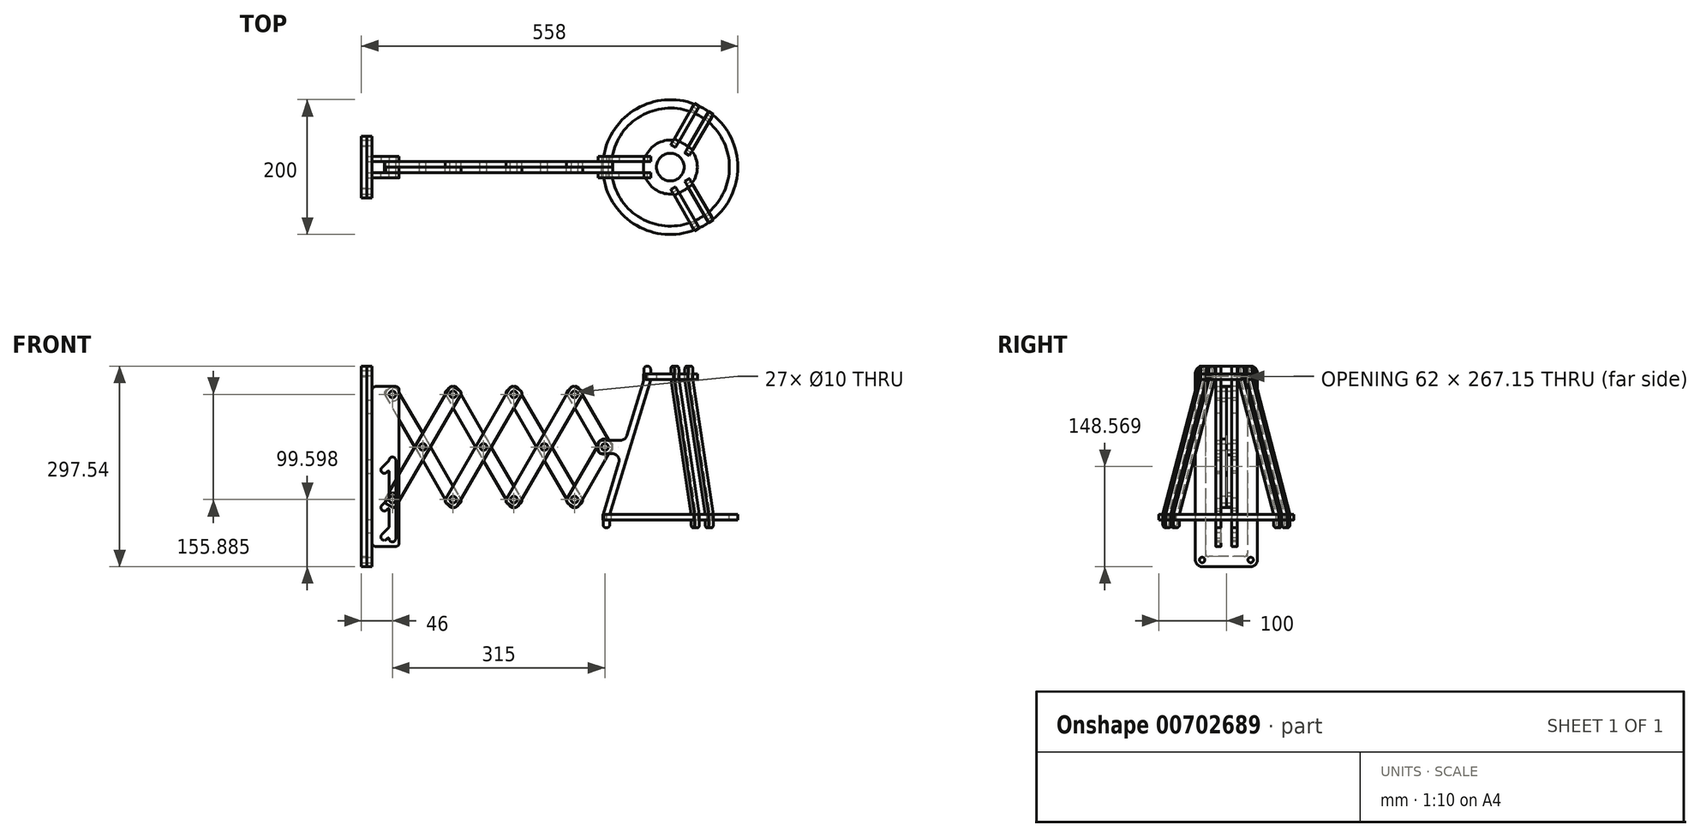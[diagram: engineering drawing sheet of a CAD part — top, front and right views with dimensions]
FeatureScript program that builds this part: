
annotation { "Feature Type Name" : "Feature", "Feature Type Description" : "" }
export const myFeature = defineFeature(function(context is Context, id is Id, definition is map)
    precondition{}
    {
        {
            var Q0;
            Q0=qCreatedBy(makeId("Front.planeOp"),FACE);
            var sketch = newSketch(context, id + "F0", { "sketchPlane" : qUnion([Q0])});
            skLineSegment(sketch, "E0.bottom", {"start": v(54.33, 84.1) * mm, "end": v(45.67, 89.1) * mm});
            skLineSegment(sketch, "E0.top", {"start": v(-45.67, -89.1) * mm, "end": v(-54.33, -84.1) * mm});
            skLineSegment(sketch, "E0.left", {"start": v(56.16, 77.27) * mm, "end": v(-38.84, -87.27) * mm});
            skLineSegment(sketch, "E0.right", {"start": v(38.84, 87.27) * mm, "end": v(-56.16, -77.27) * mm});
            skPoint(sketch, "E0.middle", {"position": v(0, 0) * mm});
            skLineSegment(sketch, "E1", {"start": v(0, 185.82) * mm, "end": v(0, -203.94) * mm, "construction": true});
            skLineSegment(sketch, "E2", {"start": v(-279.88, 0) * mm, "end": v(337.24, 0) * mm, "construction": true});
            skCircle(sketch, "E3", {"center": v(0, 0) * mm, "radius": 5 * mm});
            skCircle(sketch, "E4", {"center": v(45, 77.94) * mm, "radius": 5 * mm});
            skCircle(sketch, "E5.MirrorC", {"center": v(-45, -77.94) * mm, "radius": 5 * mm});
            skPoint(sketch, "E6.visualSharp", {"position": v(41.34, 91.6) * mm});
            skArc(sketch, "E6.filletArc", {"start": v(45.67, 89.1) * mm, "mid": v(41.88, 89.6) * mm, "end": v(38.84, 87.27) * mm});
            skPoint(sketch, "E7.visualSharp", {"position": v(58.66, 81.6) * mm});
            skArc(sketch, "E7.filletArc", {"start": v(56.16, 77.27) * mm, "mid": v(56.66, 81.07) * mm, "end": v(54.33, 84.1) * mm});
            skPoint(sketch, "E8.visualSharp", {"position": v(-41.34, -91.6) * mm});
            skArc(sketch, "E8.filletArc", {"start": v(-45.67, -89.1) * mm, "mid": v(-41.88, -89.6) * mm, "end": v(-38.84, -87.27) * mm});
            skPoint(sketch, "E9.visualSharp", {"position": v(-58.66, -81.6) * mm});
            skArc(sketch, "E9.filletArc", {"start": v(-56.16, -77.27) * mm, "mid": v(-56.66, -81.07) * mm, "end": v(-54.33, -84.1) * mm});
            skSolve(sketch);
        }
        {
            var Q0;
            Q0=makeQuery(id+"F0.imprint","IMPRINT",FACE,{"disambiguationData":[TD([[makeQuery(id+"F0.imprint","IMPRINT",EDGE,{"derivedFrom":sQuery(id+"F0.wireOp",EDGE,"E0.bottom")}),1.0]])]});
            var Q1;
            Q1=makeQuery(id+"F0.imprint","IMPRINT",FACE,{"disambiguationData":[TD([[makeQuery(id+"F0.imprint","IMPRINT",EDGE,{"derivedFrom":sQuery(id+"F0.wireOp",EDGE,"E3")}),-1.0]])]});
            var Q2;
            Q2=makeQuery(id+"F0.imprint","IMPRINT",FACE,{"disambiguationData":[TD([[makeQuery(id+"F0.imprint","IMPRINT",EDGE,{"derivedFrom":sQuery(id+"F0.wireOp",EDGE,"E0.top")}),-1.0]])]});
            var Q3;
            Q3=sQuery(id+"F0.wireOp",EDGE,"E0.right");
            var Q4;
            Q4=sQuery(id+"F0.wireOp",EDGE,"E0.left");
            extrude(context, id + "F1", {"entities" : qUnion([Q0, Q1, Q2]), "surfaceEntities" : qUnion([Q3, Q4]), "depth" : 8 * mm, "offsetDistance" : 25 * mm});
        }
        {
            var Q0;
            Q0=makeQuery(id+"F1.opExtrude","SWEPT_BODY",BODY,{"disambiguationData":[OSD([sQuery(id+"F0.wireOp",EDGE,"E0.bottom"),sQuery(id+"F0.wireOp",EDGE,"E0.top"),sQuery(id+"F0.wireOp",EDGE,"E0.left"),sQuery(id+"F0.wireOp",EDGE,"E0.right"),sQuery(id+"F0.wireOp",EDGE,"E3"),sQuery(id+"F0.wireOp",EDGE,"E4"),sQuery(id+"F0.wireOp",EDGE,"E5.MirrorC"),sQuery(id+"F0.wireOp",EDGE,"E6.filletArc"),sQuery(id+"F0.wireOp",EDGE,"E7.filletArc"),sQuery(id+"F0.wireOp",EDGE,"E8.filletArc"),sQuery(id+"F0.wireOp",EDGE,"E9.filletArc")])]});
            var Q1;
            Q1=qCreatedBy(makeId("Right.planeOp"),FACE);
            mirror(context, id + "F2", {"entities" : qUnion([Q0]), "mirrorPlane" : qUnion([Q1])});
        }
        {
            var Q0;
            Q0=makeQuery(id+"F2.opPattern","COPY",BODY,{"derivedFrom":makeQuery(id+"F1.opExtrude","SWEPT_BODY",BODY,{"disambiguationData":[OSD([sQuery(id+"F0.wireOp",EDGE,"E0.bottom"),sQuery(id+"F0.wireOp",EDGE,"E0.top"),sQuery(id+"F0.wireOp",EDGE,"E0.left"),sQuery(id+"F0.wireOp",EDGE,"E0.right"),sQuery(id+"F0.wireOp",EDGE,"E3"),sQuery(id+"F0.wireOp",EDGE,"E4"),sQuery(id+"F0.wireOp",EDGE,"E5.MirrorC"),sQuery(id+"F0.wireOp",EDGE,"E6.filletArc"),sQuery(id+"F0.wireOp",EDGE,"E7.filletArc"),sQuery(id+"F0.wireOp",EDGE,"E8.filletArc"),sQuery(id+"F0.wireOp",EDGE,"E9.filletArc")])]}),"instanceName":"1"});
            transform(context, id + "F3", {"entities" : qUnion([Q0]), "transformType" : TransformType.TRANSLATION_3D, "dx" : 0 * mm, "dy" : 8 * mm, "dz" : 0 * mm, "makeCopy" : false});
        }
        {
            var Q0;
            Q0=makeQuery(id+"F1.opExtrude","SWEPT_BODY",BODY,{"disambiguationData":[OSD([sQuery(id+"F0.wireOp",EDGE,"E0.bottom"),sQuery(id+"F0.wireOp",EDGE,"E0.top"),sQuery(id+"F0.wireOp",EDGE,"E0.left"),sQuery(id+"F0.wireOp",EDGE,"E0.right"),sQuery(id+"F0.wireOp",EDGE,"E3"),sQuery(id+"F0.wireOp",EDGE,"E4"),sQuery(id+"F0.wireOp",EDGE,"E5.MirrorC"),sQuery(id+"F0.wireOp",EDGE,"E6.filletArc"),sQuery(id+"F0.wireOp",EDGE,"E7.filletArc"),sQuery(id+"F0.wireOp",EDGE,"E8.filletArc"),sQuery(id+"F0.wireOp",EDGE,"E9.filletArc")])]});
            transform(context, id + "F4", {"entities" : qUnion([Q0]), "transformType" : TransformType.TRANSLATION_3D, "dx" : 90 * mm, "dy" : 0 * mm, "dz" : 0 * mm, "makeCopy" : true});
        }
        {
            var Q0;
            Q0=makeQuery(id+"F2.opPattern","COPY",BODY,{"derivedFrom":makeQuery(id+"F1.opExtrude","SWEPT_BODY",BODY,{"disambiguationData":[OSD([sQuery(id+"F0.wireOp",EDGE,"E0.bottom"),sQuery(id+"F0.wireOp",EDGE,"E0.top"),sQuery(id+"F0.wireOp",EDGE,"E0.left"),sQuery(id+"F0.wireOp",EDGE,"E0.right"),sQuery(id+"F0.wireOp",EDGE,"E3"),sQuery(id+"F0.wireOp",EDGE,"E4"),sQuery(id+"F0.wireOp",EDGE,"E5.MirrorC"),sQuery(id+"F0.wireOp",EDGE,"E6.filletArc"),sQuery(id+"F0.wireOp",EDGE,"E7.filletArc"),sQuery(id+"F0.wireOp",EDGE,"E8.filletArc"),sQuery(id+"F0.wireOp",EDGE,"E9.filletArc")])]}),"instanceName":"1"});
            transform(context, id + "F5", {"entities" : qUnion([Q0]), "transformType" : TransformType.TRANSLATION_3D, "dx" : -90 * mm, "dy" : 0 * mm, "dz" : 0 * mm, "makeCopy" : true});
        }
        {
            var Q0;
            Q0=makeQuery(id+"F1.opExtrude","SWEPT_BODY",BODY,{"disambiguationData":[OSD([sQuery(id+"F0.wireOp",EDGE,"E0.bottom"),sQuery(id+"F0.wireOp",EDGE,"E0.top"),sQuery(id+"F0.wireOp",EDGE,"E0.left"),sQuery(id+"F0.wireOp",EDGE,"E0.right"),sQuery(id+"F0.wireOp",EDGE,"E3"),sQuery(id+"F0.wireOp",EDGE,"E4"),sQuery(id+"F0.wireOp",EDGE,"E5.MirrorC"),sQuery(id+"F0.wireOp",EDGE,"E6.filletArc"),sQuery(id+"F0.wireOp",EDGE,"E7.filletArc"),sQuery(id+"F0.wireOp",EDGE,"E8.filletArc"),sQuery(id+"F0.wireOp",EDGE,"E9.filletArc")])]});
            transform(context, id + "F6", {"entities" : qUnion([Q0]), "transformType" : TransformType.TRANSLATION_3D, "dx" : -90 * mm, "dy" : 0 * mm, "dz" : 0 * mm, "makeCopy" : true});
        }
        {
            var Q0;
            Q0=makeQuery(id+"F2.opPattern","COPY",BODY,{"derivedFrom":makeQuery(id+"F1.opExtrude","SWEPT_BODY",BODY,{"disambiguationData":[OSD([sQuery(id+"F0.wireOp",EDGE,"E0.bottom"),sQuery(id+"F0.wireOp",EDGE,"E0.top"),sQuery(id+"F0.wireOp",EDGE,"E0.left"),sQuery(id+"F0.wireOp",EDGE,"E0.right"),sQuery(id+"F0.wireOp",EDGE,"E3"),sQuery(id+"F0.wireOp",EDGE,"E4"),sQuery(id+"F0.wireOp",EDGE,"E5.MirrorC"),sQuery(id+"F0.wireOp",EDGE,"E6.filletArc"),sQuery(id+"F0.wireOp",EDGE,"E7.filletArc"),sQuery(id+"F0.wireOp",EDGE,"E8.filletArc"),sQuery(id+"F0.wireOp",EDGE,"E9.filletArc")])]}),"instanceName":"1"});
            transform(context, id + "F7", {"entities" : qUnion([Q0]), "transformType" : TransformType.TRANSLATION_3D, "dx" : 90 * mm, "dy" : 0 * mm, "dz" : 0 * mm, "makeCopy" : true});
        }
        {
            var Q0;
            Q0=makeQuery(id+"F7.opPattern","COPY",FACE,{"derivedFrom":makeQuery(id+"F2.opPattern","COPY",FACE,{"derivedFrom":makeQuery(id+"F1.opExtrude","CAP_FACE",FACE,{"disambiguationData":[OSD([sQuery(id+"F0.wireOp",EDGE,"E0.bottom"),sQuery(id+"F0.wireOp",EDGE,"E0.top"),sQuery(id+"F0.wireOp",EDGE,"E0.left"),sQuery(id+"F0.wireOp",EDGE,"E0.right"),sQuery(id+"F0.wireOp",EDGE,"E3"),sQuery(id+"F0.wireOp",EDGE,"E4"),sQuery(id+"F0.wireOp",EDGE,"E5.MirrorC"),sQuery(id+"F0.wireOp",EDGE,"E6.filletArc"),sQuery(id+"F0.wireOp",EDGE,"E7.filletArc"),sQuery(id+"F0.wireOp",EDGE,"E8.filletArc"),sQuery(id+"F0.wireOp",EDGE,"E9.filletArc")])],"isStart":true}),"instanceName":"1"}),"instanceName":"1"});
            var sketch = newSketch(context, id + "F8", { "sketchPlane" : qUnion([Q0])});
            skCircle(sketch, "E10.0", {"center": v(135, 77.94) * mm, "radius": 5 * mm});
            skLineSegment(sketch, "E11", {"start": v(130, 89.6) * mm, "end": v(160, 89.6) * mm, "construction": true});
            skPoint(sketch, "E11.startSnap0", {"position": v(41.88, 89.6) * mm});
            skLineSegment(sketch, "E12", {"start": v(22.72, 0) * mm, "end": v(188.2, 0) * mm, "construction": true});
            skLineSegment(sketch, "E13", {"start": v(130, 89.6) * mm, "end": v(160, 89.6) * mm});
            skLineSegment(sketch, "E14", {"start": v(135, 121.8) * mm, "end": v(135, -172.81) * mm, "construction": true});
            skArc(sketch, "E15.0", {"start": v(140, -20) * mm, "mid": v(135, -15) * mm, "end": v(130, -20) * mm});
            skLineSegment(sketch, "E16", {"start": v(95.12, -77.94) * mm, "end": v(188.2, -77.94) * mm, "construction": true});
            skArc(sketch, "E17.MirrorC", {"start": v(140, -135.88) * mm, "mid": v(135, -140.88) * mm, "end": v(130, -135.88) * mm});
            skLineSegment(sketch, "E18", {"start": v(130, -147.54) * mm, "end": v(160, -147.54) * mm});
            skLineSegment(sketch, "E19", {"start": v(125, 84.6) * mm, "end": v(125, -142.54) * mm});
            skLineSegment(sketch, "E20", {"start": v(165, 84.6) * mm, "end": v(165, 69.6) * mm});
            skLineSegment(sketch, "E21", {"start": v(130, -135.88) * mm, "end": v(130, -20) * mm});
            skLineSegment(sketch, "E22.MirrorCS", {"start": v(140, -119.33) * mm, "end": v(140, -92.37) * mm});
            skPoint(sketch, "E23.newPointB", {"position": v(24.22, 89.6) * mm});
            skArc(sketch, "E23.filletArc", {"start": v(130, 89.6) * mm, "mid": v(126.46, 88.14) * mm, "end": v(125, 84.6) * mm});
            skPoint(sketch, "E24.newPointA", {"position": v(188.2, 89.6) * mm});
            skArc(sketch, "E24.filletArc", {"start": v(165, 84.6) * mm, "mid": v(163.54, 88.14) * mm, "end": v(160, 89.6) * mm});
            skPoint(sketch, "E25.visualSharp", {"position": v(125, -147.54) * mm});
            skArc(sketch, "E25.filletArc", {"start": v(125, -142.54) * mm, "mid": v(126.46, -146.08) * mm, "end": v(130, -147.54) * mm});
            skPoint(sketch, "E26.visualSharp", {"position": v(165, -147.54) * mm});
            skArc(sketch, "E26.filletArc", {"start": v(160, -147.54) * mm, "mid": v(163.54, -146.08) * mm, "end": v(165, -142.54) * mm});
            skLineSegment(sketch, "E27", {"start": v(165, 69.6) * mm, "end": v(173, 69.6) * mm});
            skLineSegment(sketch, "E28", {"start": v(173, 69.6) * mm, "end": v(173, 49.6) * mm});
            skLineSegment(sketch, "E29", {"start": v(173, 49.6) * mm, "end": v(165, 49.6) * mm});
            skLineSegment(sketch, "E30", {"start": v(165, -107.54) * mm, "end": v(173, -107.54) * mm});
            skLineSegment(sketch, "E31", {"start": v(173, -107.54) * mm, "end": v(173, -127.54) * mm});
            skLineSegment(sketch, "E32", {"start": v(173, -127.54) * mm, "end": v(165, -127.54) * mm});
            skLineSegment(sketch, "E33.trimOffspring", {"start": v(165, -127.54) * mm, "end": v(165, -142.54) * mm});
            skLineSegment(sketch, "E34.trimOffspring", {"start": v(165, 49.6) * mm, "end": v(165, -18.97) * mm});
            skLineSegment(sketch, "E35", {"start": v(165, -18.97) * mm, "end": v(173, -18.97) * mm});
            skLineSegment(sketch, "E36", {"start": v(173, -18.97) * mm, "end": v(173, -38.97) * mm});
            skLineSegment(sketch, "E37", {"start": v(173, -38.97) * mm, "end": v(165, -38.97) * mm});
            skLineSegment(sketch, "E38.trimOffspring", {"start": v(165, -38.97) * mm, "end": v(165, -107.54) * mm});
            skPoint(sketch, "E39.orphan", {"position": v(165, -28.97) * mm});
            skArc(sketch, "E40", {"start": v(143.5, -93.46) * mm, "mid": v(150.57, -93.46) * mm, "end": v(150.57, -86.4) * mm});
            skLineSegment(sketch, "E41", {"start": v(150.57, -86.4) * mm, "end": v(140, -75.82) * mm});
            skLineSegment(sketch, "E42.MirrorCS", {"start": v(143.5, -93.46) * mm, "end": v(141.7, -91.67) * mm});
            skArc(sketch, "E43.filletArc", {"start": v(141.7, -91.67) * mm, "mid": v(140.62, -91.45) * mm, "end": v(140, -92.37) * mm});
            skArc(sketch, "E44", {"start": v(143.5, -136.97) * mm, "mid": v(150.57, -136.97) * mm, "end": v(150.57, -129.9) * mm});
            skLineSegment(sketch, "E45", {"start": v(150.57, -129.9) * mm, "end": v(140, -119.33) * mm});
            skLineSegment(sketch, "E46.MirrorCS", {"start": v(143.5, -136.97) * mm, "end": v(141.7, -135.18) * mm});
            skArc(sketch, "E47.filletArc", {"start": v(141.7, -135.18) * mm, "mid": v(140.62, -134.96) * mm, "end": v(140, -135.88) * mm});
            skArc(sketch, "E48", {"start": v(143.5, -37.65) * mm, "mid": v(150.57, -37.65) * mm, "end": v(150.57, -30.57) * mm});
            skLineSegment(sketch, "E49", {"start": v(150.57, -30.57) * mm, "end": v(140, -20) * mm});
            skLineSegment(sketch, "E50.MirrorCS", {"start": v(143.5, -37.65) * mm, "end": v(141.7, -35.85) * mm});
            skArc(sketch, "E51.filletArc", {"start": v(141.7, -35.85) * mm, "mid": v(140.62, -35.63) * mm, "end": v(140, -36.56) * mm});
            skLineSegment(sketch, "E52.trimOffspring", {"start": v(140, -75.82) * mm, "end": v(140, -36.56) * mm});
            skSolve(sketch);
        }
        {
            var Q0;
            Q0=qSketchRegion(id+"F8",true);
            extrude(context, id + "F9", {"entities" : qUnion([Q0]), "depth" : 8 * mm, "offsetDistance" : 25 * mm});
        }
        {
            var Q0;
            Q0=makeQuery(id+"F9.opExtrude","SWEPT_BODY",BODY,{"disambiguationData":[OSD([sQuery(id+"F8.wireOp",EDGE,"E10.0"),sQuery(id+"F8.wireOp",EDGE,"E13"),sQuery(id+"F8.wireOp",EDGE,"E15.0"),sQuery(id+"F8.wireOp",EDGE,"E17.MirrorC"),sQuery(id+"F8.wireOp",EDGE,"E18"),sQuery(id+"F8.wireOp",EDGE,"E19"),sQuery(id+"F8.wireOp",EDGE,"E20"),sQuery(id+"F8.wireOp",EDGE,"E21"),sQuery(id+"F8.wireOp",EDGE,"E22.MirrorCS"),sQuery(id+"F8.wireOp",EDGE,"E23.filletArc"),sQuery(id+"F8.wireOp",EDGE,"E24.filletArc"),sQuery(id+"F8.wireOp",EDGE,"E25.filletArc"),sQuery(id+"F8.wireOp",EDGE,"E26.filletArc")])]});
            var Q1;
            Q1=qCreatedBy(makeId("Front.planeOp"),FACE);
            mirror(context, id + "F10", {"entities" : qUnion([Q0]), "mirrorPlane" : qUnion([Q1])});
        }
        {
            var Q0;
            Q0=makeQuery(id+"F9.opExtrude","SWEPT_FACE",FACE,{"disambiguationData":[OSD([sQuery(id+"F8.wireOp",EDGE,"E34.trimOffspring")])]});
            var sketch = newSketch(context, id + "F11", { "sketchPlane" : qUnion([Q0])});
            skPoint(sketch, "E53.middle", {"position": v(0, 0) * mm});
            skLineSegment(sketch, "E54.0.0", {"start": v(-8, 49.6) * mm, "end": v(-8, 69.6) * mm});
            skLineSegment(sketch, "E54.0.1", {"start": v(-8, 69.6) * mm, "end": v(-16, 69.6) * mm});
            skLineSegment(sketch, "E54.0.2", {"start": v(-16, 69.6) * mm, "end": v(-16, 49.6) * mm});
            skLineSegment(sketch, "E54.0.3", {"start": v(-16, 49.6) * mm, "end": v(-8, 49.6) * mm});
            skLineSegment(sketch, "E55.0.0", {"start": v(8, 69.6) * mm, "end": v(8, 49.6) * mm});
            skLineSegment(sketch, "E55.0.1", {"start": v(8, 49.6) * mm, "end": v(16, 49.6) * mm});
            skLineSegment(sketch, "E55.0.2", {"start": v(16, 49.6) * mm, "end": v(16, 69.6) * mm});
            skLineSegment(sketch, "E55.0.3", {"start": v(16, 69.6) * mm, "end": v(8, 69.6) * mm});
            skLineSegment(sketch, "E56.0.0", {"start": v(-8, -38.97) * mm, "end": v(-8, -18.97) * mm});
            skLineSegment(sketch, "E56.0.1", {"start": v(-8, -18.97) * mm, "end": v(-16, -18.97) * mm});
            skLineSegment(sketch, "E56.0.2", {"start": v(-16, -18.97) * mm, "end": v(-16, -38.97) * mm});
            skLineSegment(sketch, "E56.0.3", {"start": v(-16, -38.97) * mm, "end": v(-8, -38.97) * mm});
            skLineSegment(sketch, "E57.0.0", {"start": v(8, -18.97) * mm, "end": v(8, -38.97) * mm});
            skLineSegment(sketch, "E57.0.1", {"start": v(8, -38.97) * mm, "end": v(16, -38.97) * mm});
            skLineSegment(sketch, "E57.0.2", {"start": v(16, -38.97) * mm, "end": v(16, -18.97) * mm});
            skLineSegment(sketch, "E57.0.3", {"start": v(16, -18.97) * mm, "end": v(8, -18.97) * mm});
            skLineSegment(sketch, "E58.0.0", {"start": v(-8, -127.54) * mm, "end": v(-8, -107.54) * mm});
            skLineSegment(sketch, "E58.0.1", {"start": v(-8, -107.54) * mm, "end": v(-16, -107.54) * mm});
            skLineSegment(sketch, "E58.0.2", {"start": v(-16, -107.54) * mm, "end": v(-16, -127.54) * mm});
            skLineSegment(sketch, "E58.0.3", {"start": v(-16, -127.54) * mm, "end": v(-8, -127.54) * mm});
            skLineSegment(sketch, "E59.0.0", {"start": v(8, -107.54) * mm, "end": v(8, -127.54) * mm});
            skLineSegment(sketch, "E59.0.1", {"start": v(8, -127.54) * mm, "end": v(16, -127.54) * mm});
            skLineSegment(sketch, "E59.0.2", {"start": v(16, -127.54) * mm, "end": v(16, -107.54) * mm});
            skLineSegment(sketch, "E59.0.3", {"start": v(16, -107.54) * mm, "end": v(8, -107.54) * mm});
            skLineSegment(sketch, "E60", {"start": v(46, 109.6) * mm, "end": v(46, -167.54) * mm});
            skLineSegment(sketch, "E61", {"start": v(-36, 119.6) * mm, "end": v(36, 119.6) * mm});
            skLineSegment(sketch, "E62", {"start": v(-36, -177.54) * mm, "end": v(36, -177.54) * mm});
            skLineSegment(sketch, "E63.MirrorCS", {"start": v(-46, 109.6) * mm, "end": v(-46, -167.54) * mm});
            skPoint(sketch, "E64.visualSharp", {"position": v(-46, 119.6) * mm});
            skArc(sketch, "E64.filletArc", {"start": v(-36, 119.6) * mm, "mid": v(-43.07, 116.67) * mm, "end": v(-46, 109.6) * mm});
            skPoint(sketch, "E65.visualSharp", {"position": v(46, 119.6) * mm});
            skArc(sketch, "E65.filletArc", {"start": v(46, 109.6) * mm, "mid": v(43.07, 116.67) * mm, "end": v(36, 119.6) * mm});
            skPoint(sketch, "E66.visualSharp", {"position": v(-46, -177.54) * mm});
            skArc(sketch, "E66.filletArc", {"start": v(-46, -167.54) * mm, "mid": v(-43.07, -174.62) * mm, "end": v(-36, -177.54) * mm});
            skPoint(sketch, "E67.visualSharp", {"position": v(46, -177.54) * mm});
            skArc(sketch, "E67.filletArc", {"start": v(36, -177.54) * mm, "mid": v(43.07, -174.62) * mm, "end": v(46, -167.54) * mm});
            skCircle(sketch, "E68", {"center": v(-36, 109.6) * mm, "radius": 4 * mm});
            skCircle(sketch, "E69", {"center": v(36, 109.6) * mm, "radius": 4 * mm});
            skCircle(sketch, "E70", {"center": v(-36, -167.54) * mm, "radius": 4 * mm});
            skCircle(sketch, "E71", {"center": v(36, -167.54) * mm, "radius": 4 * mm});
            skSolve(sketch);
        }
        {
            var Q0;
            Q0=qSketchRegion(id+"F11",true);
            extrude(context, id + "F12", {"entities" : qUnion([Q0]), "depth" : 8 * mm, "offsetDistance" : 25 * mm});
        }
        {
            var Q0;
            Q0=makeQuery(id+"F12.opExtrude","CAP_FACE",FACE,{"disambiguationData":[OSD([sQuery(id+"F11.wireOp",EDGE,"E54.0.0"),sQuery(id+"F11.wireOp",EDGE,"E54.0.1"),sQuery(id+"F11.wireOp",EDGE,"E54.0.2"),sQuery(id+"F11.wireOp",EDGE,"E54.0.3"),sQuery(id+"F11.wireOp",EDGE,"E55.0.0"),sQuery(id+"F11.wireOp",EDGE,"E55.0.1"),sQuery(id+"F11.wireOp",EDGE,"E55.0.2"),sQuery(id+"F11.wireOp",EDGE,"E55.0.3"),sQuery(id+"F11.wireOp",EDGE,"E56.0.0"),sQuery(id+"F11.wireOp",EDGE,"E56.0.1"),sQuery(id+"F11.wireOp",EDGE,"E56.0.2"),sQuery(id+"F11.wireOp",EDGE,"E56.0.3"),sQuery(id+"F11.wireOp",EDGE,"E57.0.0"),sQuery(id+"F11.wireOp",EDGE,"E57.0.1"),sQuery(id+"F11.wireOp",EDGE,"E57.0.2"),sQuery(id+"F11.wireOp",EDGE,"E57.0.3"),sQuery(id+"F11.wireOp",EDGE,"E58.0.0"),sQuery(id+"F11.wireOp",EDGE,"E58.0.1"),sQuery(id+"F11.wireOp",EDGE,"E58.0.2"),sQuery(id+"F11.wireOp",EDGE,"E58.0.3"),sQuery(id+"F11.wireOp",EDGE,"E59.0.0"),sQuery(id+"F11.wireOp",EDGE,"E59.0.1"),sQuery(id+"F11.wireOp",EDGE,"E59.0.2"),sQuery(id+"F11.wireOp",EDGE,"E59.0.3"),sQuery(id+"F11.wireOp",EDGE,"E60"),sQuery(id+"F11.wireOp",EDGE,"E61"),sQuery(id+"F11.wireOp",EDGE,"E62"),sQuery(id+"F11.wireOp",EDGE,"E63.MirrorCS"),sQuery(id+"F11.wireOp",EDGE,"E64.filletArc"),sQuery(id+"F11.wireOp",EDGE,"E65.filletArc"),sQuery(id+"F11.wireOp",EDGE,"E66.filletArc"),sQuery(id+"F11.wireOp",EDGE,"E67.filletArc"),sQuery(id+"F11.wireOp",EDGE,"E68"),sQuery(id+"F11.wireOp",EDGE,"E69"),sQuery(id+"F11.wireOp",EDGE,"E70"),sQuery(id+"F11.wireOp",EDGE,"E71")])],"isStart":false});
            var sketch = newSketch(context, id + "F13", { "sketchPlane" : qUnion([Q0])});
            skArc(sketch, "E72.0.0", {"start": v(-36, 119.6) * mm, "mid": v(-43.07, 116.67) * mm, "end": v(-46, 109.6) * mm});
            skLineSegment(sketch, "E72.0.1", {"start": v(-46, 109.6) * mm, "end": v(-46, -167.54) * mm});
            skArc(sketch, "E72.0.2", {"start": v(-46, -167.54) * mm, "mid": v(-43.07, -174.62) * mm, "end": v(-36, -177.54) * mm});
            skLineSegment(sketch, "E72.0.3", {"start": v(-36, -177.54) * mm, "end": v(36, -177.54) * mm});
            skArc(sketch, "E72.0.4", {"start": v(36, -177.54) * mm, "mid": v(43.07, -174.62) * mm, "end": v(46, -167.54) * mm});
            skLineSegment(sketch, "E72.0.5", {"start": v(46, -167.54) * mm, "end": v(46, 109.6) * mm});
            skArc(sketch, "E72.0.6", {"start": v(46, 109.6) * mm, "mid": v(43.07, 116.67) * mm, "end": v(36, 119.6) * mm});
            skLineSegment(sketch, "E72.0.7", {"start": v(36, 119.6) * mm, "end": v(-36, 119.6) * mm});
            skCircle(sketch, "E73.0", {"center": v(-36, 109.6) * mm, "radius": 4 * mm});
            skCircle(sketch, "E74.0", {"center": v(36, 109.6) * mm, "radius": 4 * mm});
            skCircle(sketch, "E75.0", {"center": v(-36, -167.54) * mm, "radius": 4 * mm});
            skCircle(sketch, "E76.0", {"center": v(36, -167.54) * mm, "radius": 4 * mm});
            skLineSegment(sketch, "E77.bottom", {"start": v(-26, 104.6) * mm, "end": v(26, 104.6) * mm});
            skLineSegment(sketch, "E77.top", {"start": v(-26, -162.54) * mm, "end": v(26, -162.54) * mm});
            skLineSegment(sketch, "E77.left", {"start": v(-31, 99.6) * mm, "end": v(-31, -157.54) * mm});
            skLineSegment(sketch, "E77.right", {"start": v(31, 99.6) * mm, "end": v(31, -157.54) * mm});
            skPoint(sketch, "E78.visualSharp", {"position": v(-31, 104.6) * mm});
            skArc(sketch, "E78.filletArc", {"start": v(-26, 104.6) * mm, "mid": v(-29.54, 103.14) * mm, "end": v(-31, 99.6) * mm});
            skPoint(sketch, "E79.visualSharp", {"position": v(31, 104.6) * mm});
            skArc(sketch, "E79.filletArc", {"start": v(31, 99.6) * mm, "mid": v(29.54, 103.14) * mm, "end": v(26, 104.6) * mm});
            skPoint(sketch, "E80.visualSharp", {"position": v(-31, -162.54) * mm});
            skArc(sketch, "E80.filletArc", {"start": v(-31, -157.54) * mm, "mid": v(-29.54, -161.08) * mm, "end": v(-26, -162.54) * mm});
            skPoint(sketch, "E81.visualSharp", {"position": v(31, -162.54) * mm});
            skArc(sketch, "E81.filletArc", {"start": v(26, -162.54) * mm, "mid": v(29.54, -161.08) * mm, "end": v(31, -157.54) * mm});
            skSolve(sketch);
        }
        {
            var Q0;
            Q0=qSketchRegion(id+"F13",true);
            extrude(context, id + "F14", {"entities" : qUnion([Q0]), "depth" : 8 * mm, "offsetDistance" : 25 * mm});
        }
        {
            var Q0;
            Q0=makeQuery(id+"F6.opPattern","COPY",FACE,{"derivedFrom":makeQuery(id+"F1.opExtrude","CAP_FACE",FACE,{"disambiguationData":[OSD([sQuery(id+"F0.wireOp",EDGE,"E0.bottom"),sQuery(id+"F0.wireOp",EDGE,"E0.top"),sQuery(id+"F0.wireOp",EDGE,"E0.left"),sQuery(id+"F0.wireOp",EDGE,"E0.right"),sQuery(id+"F0.wireOp",EDGE,"E3"),sQuery(id+"F0.wireOp",EDGE,"E4"),sQuery(id+"F0.wireOp",EDGE,"E5.MirrorC"),sQuery(id+"F0.wireOp",EDGE,"E6.filletArc"),sQuery(id+"F0.wireOp",EDGE,"E7.filletArc"),sQuery(id+"F0.wireOp",EDGE,"E8.filletArc"),sQuery(id+"F0.wireOp",EDGE,"E9.filletArc")])],"isStart":true}),"instanceName":"1"});
            var sketch = newSketch(context, id + "F15", { "sketchPlane" : qUnion([Q0])});
            skCircle(sketch, "E82.0", {"center": v(135, -77.94) * mm, "radius": 5 * mm});
            skCircle(sketch, "E83", {"center": v(135, -77.94) * mm, "radius": 10 * mm});
            skSolve(sketch);
        }
        {
            var Q0;
            Q0=qSketchRegion(id+"F15",true);
            extrude(context, id + "F16", {"entities" : qUnion([Q0]), "depth" : 8 * mm, "offsetDistance" : 25 * mm});
        }
        {
            var Q0;
            Q0=makeQuery(id+"F5.opPattern","COPY",FACE,{"derivedFrom":makeQuery(id+"F2.opPattern","COPY",FACE,{"derivedFrom":makeQuery(id+"F1.opExtrude","CAP_FACE",FACE,{"disambiguationData":[OSD([sQuery(id+"F0.wireOp",EDGE,"E0.bottom"),sQuery(id+"F0.wireOp",EDGE,"E0.top"),sQuery(id+"F0.wireOp",EDGE,"E0.left"),sQuery(id+"F0.wireOp",EDGE,"E0.right"),sQuery(id+"F0.wireOp",EDGE,"E3"),sQuery(id+"F0.wireOp",EDGE,"E4"),sQuery(id+"F0.wireOp",EDGE,"E5.MirrorC"),sQuery(id+"F0.wireOp",EDGE,"E6.filletArc"),sQuery(id+"F0.wireOp",EDGE,"E7.filletArc"),sQuery(id+"F0.wireOp",EDGE,"E8.filletArc"),sQuery(id+"F0.wireOp",EDGE,"E9.filletArc")])],"isStart":false}),"instanceName":"1"}),"instanceName":"1"});
            var sketch = newSketch(context, id + "F17", { "sketchPlane" : qUnion([Q0])});
            skCircle(sketch, "E84.0", {"center": v(-135, 77.94) * mm, "radius": 5 * mm});
            skCircle(sketch, "E85", {"center": v(-135, 77.94) * mm, "radius": 10 * mm});
            skSolve(sketch);
        }
        {
            var Q0;
            Q0=qSketchRegion(id+"F17",true);
            extrude(context, id + "F18", {"entities" : qUnion([Q0]), "depth" : 8 * mm, "offsetDistance" : 25 * mm});
        }
        {
            var Q0;
            Q0=makeQuery(id+"F2.opPattern","COPY",FACE,{"derivedFrom":makeQuery(id+"F1.opExtrude","CAP_FACE",FACE,{"disambiguationData":[OSD([sQuery(id+"F0.wireOp",EDGE,"E0.bottom"),sQuery(id+"F0.wireOp",EDGE,"E0.top"),sQuery(id+"F0.wireOp",EDGE,"E0.left"),sQuery(id+"F0.wireOp",EDGE,"E0.right"),sQuery(id+"F0.wireOp",EDGE,"E3"),sQuery(id+"F0.wireOp",EDGE,"E4"),sQuery(id+"F0.wireOp",EDGE,"E5.MirrorC"),sQuery(id+"F0.wireOp",EDGE,"E6.filletArc"),sQuery(id+"F0.wireOp",EDGE,"E7.filletArc"),sQuery(id+"F0.wireOp",EDGE,"E8.filletArc"),sQuery(id+"F0.wireOp",EDGE,"E9.filletArc")])],"isStart":false}),"instanceName":"1"});
            var sketch = newSketch(context, id + "F19", { "sketchPlane" : qUnion([Q0])});
            skLineSegment(sketch, "E86.top", {"start": v(134.33, -89.1) * mm, "end": v(125.67, -84.1) * mm});
            skLineSegment(sketch, "E86.left", {"start": v(191.55, 0) * mm, "end": v(141.16, -87.27) * mm});
            skLineSegment(sketch, "E86.right", {"start": v(173.84, 9.33) * mm, "end": v(123.84, -77.27) * mm});
            skPoint(sketch, "E86.middle", {"position": v(180, 0) * mm});
            skLineSegment(sketch, "E87", {"start": v(180, 185.82) * mm, "end": v(180, -203.94) * mm, "construction": true});
            skLineSegment(sketch, "E88", {"start": v(-99.88, 0) * mm, "end": v(517.24, 0) * mm, "construction": true});
            skCircle(sketch, "E89.MirrorC", {"center": v(135, -77.94) * mm, "radius": 5 * mm});
            skPoint(sketch, "E90.visualSharp", {"position": v(138.66, -91.6) * mm});
            skArc(sketch, "E90.filletArc", {"start": v(134.33, -89.1) * mm, "mid": v(138.12, -89.6) * mm, "end": v(141.16, -87.27) * mm});
            skPoint(sketch, "E91.visualSharp", {"position": v(121.34, -81.6) * mm});
            skArc(sketch, "E91.filletArc", {"start": v(123.84, -77.27) * mm, "mid": v(123.34, -81.07) * mm, "end": v(125.67, -84.1) * mm});
            skLineSegment(sketch, "E92.bottom", {"start": v(189.33, 6.16) * mm, "end": v(180.67, 11.16) * mm});
            skCircle(sketch, "E93", {"center": v(180, 0) * mm, "radius": 5 * mm});
            skArc(sketch, "E94.filletArc", {"start": v(180.67, 11.16) * mm, "mid": v(176.88, 11.66) * mm, "end": v(173.84, 9.33) * mm});
            skArc(sketch, "E95.filletArc", {"start": v(191.16, -0.67) * mm, "mid": v(191.66, 3.12) * mm, "end": v(189.33, 6.16) * mm});
            skSolve(sketch);
        }
        {
            var Q0;
            Q0=qSketchRegion(id+"F19",true);
            extrude(context, id + "F20", {"entities" : qUnion([Q0]), "operationType" : NewBodyOperationType.ADD, "depth" : 8 * mm, "offsetDistance" : 25 * mm});
        }
        {
            var Q0;
            Q0=makeQuery(id+"F4.opPattern","COPY",FACE,{"derivedFrom":makeQuery(id+"F1.opExtrude","CAP_FACE",FACE,{"disambiguationData":[OSD([sQuery(id+"F0.wireOp",EDGE,"E0.bottom"),sQuery(id+"F0.wireOp",EDGE,"E0.top"),sQuery(id+"F0.wireOp",EDGE,"E0.left"),sQuery(id+"F0.wireOp",EDGE,"E0.right"),sQuery(id+"F0.wireOp",EDGE,"E3"),sQuery(id+"F0.wireOp",EDGE,"E4"),sQuery(id+"F0.wireOp",EDGE,"E5.MirrorC"),sQuery(id+"F0.wireOp",EDGE,"E6.filletArc"),sQuery(id+"F0.wireOp",EDGE,"E7.filletArc"),sQuery(id+"F0.wireOp",EDGE,"E8.filletArc"),sQuery(id+"F0.wireOp",EDGE,"E9.filletArc")])],"isStart":true}),"instanceName":"1"});
            var sketch = newSketch(context, id + "F21", { "sketchPlane" : qUnion([Q0])});
            skLineSegment(sketch, "E96.top", {"start": v(-180.67, -11.16) * mm, "end": v(-189.33, -6.16) * mm});
            skLineSegment(sketch, "E96.left", {"start": v(-123.45, 77.94) * mm, "end": v(-173.84, -9.33) * mm});
            skLineSegment(sketch, "E96.right", {"start": v(-141.16, 87.27) * mm, "end": v(-191.16, 0.67) * mm});
            skPoint(sketch, "E96.middle", {"position": v(-135, 77.94) * mm});
            skLineSegment(sketch, "E97", {"start": v(-135, 263.76) * mm, "end": v(-135, -126) * mm, "construction": true});
            skLineSegment(sketch, "E98", {"start": v(-414.88, 77.94) * mm, "end": v(202.24, 77.94) * mm, "construction": true});
            skCircle(sketch, "E99.MirrorC", {"center": v(-180, 0) * mm, "radius": 5 * mm});
            skPoint(sketch, "E100.visualSharp", {"position": v(-176.34, -13.66) * mm});
            skArc(sketch, "E100.filletArc", {"start": v(-180.67, -11.16) * mm, "mid": v(-176.88, -11.66) * mm, "end": v(-173.84, -9.33) * mm});
            skPoint(sketch, "E101.visualSharp", {"position": v(-193.66, -3.66) * mm});
            skArc(sketch, "E101.filletArc", {"start": v(-191.16, 0.67) * mm, "mid": v(-191.66, -3.12) * mm, "end": v(-189.33, -6.16) * mm});
            skLineSegment(sketch, "E102.bottom", {"start": v(-125.67, 84.1) * mm, "end": v(-134.33, 89.1) * mm});
            skCircle(sketch, "E103", {"center": v(-135, 77.94) * mm, "radius": 5 * mm});
            skArc(sketch, "E104.filletArc", {"start": v(-134.33, 89.1) * mm, "mid": v(-138.12, 89.6) * mm, "end": v(-141.16, 87.27) * mm});
            skArc(sketch, "E105.filletArc", {"start": v(-123.84, 77.27) * mm, "mid": v(-123.34, 81.07) * mm, "end": v(-125.67, 84.1) * mm});
            skSolve(sketch);
        }
        {
            var Q0;
            Q0=qSketchRegion(id+"F21",true);
            extrude(context, id + "F22", {"entities" : qUnion([Q0]), "depth" : 8 * mm, "offsetDistance" : 25 * mm});
        }
        {
            var Q0;
            Q0=qCreatedBy(makeId("Top.planeOp"),FACE);
            cPlane(context, id + "F23", {"entities" : qUnion([Q0]), "cplaneType" : CPlaneType.OFFSET, "offset" : 100 * mm, "width" : 150 * mm, "height" : 150 * mm});
        }
        {
            var Q0;
            Q0=qCreatedBy(id+"F23.planeOp",FACE);
            var sketch = newSketch(context, id + "F24", { "sketchPlane" : qUnion([Q0])});
            skLineSegment(sketch, "E106", {"start": v(275, -71.82) * mm, "end": v(275, 43.7) * mm, "construction": true});
            skCircle(sketch, "E107", {"center": v(275, 0) * mm, "radius": 20.5 * mm});
            skLineSegment(sketch, "E108", {"start": v(166.47, 0) * mm, "end": v(330.06, 0) * mm, "construction": true});
            skLineSegment(sketch, "E109", {"start": v(235.8, -8) * mm, "end": v(240.8, -8) * mm});
            skLineSegment(sketch, "E110", {"start": v(240.8, -8) * mm, "end": v(240.8, -16) * mm});
            skLineSegment(sketch, "E111", {"start": v(240.8, -16) * mm, "end": v(238.34, -16) * mm});
            skLineSegment(sketch, "E112.MirrorCS", {"start": v(235.8, 8) * mm, "end": v(240.8, 8) * mm});
            skLineSegment(sketch, "E113.MirrorCS", {"start": v(240.8, 8) * mm, "end": v(240.8, 16) * mm});
            skLineSegment(sketch, "E114.MirrorCS", {"start": v(240.8, 16) * mm, "end": v(238.34, 16) * mm});
            skLineSegment(sketch, "E115.1.1", {"start": v(285.17, -33.61) * mm, "end": v(278.24, -37.61) * mm});
            skLineSegment(sketch, "E115.1.2", {"start": v(287.67, -37.94) * mm, "end": v(285.17, -33.61) * mm});
            skLineSegment(sketch, "E115.1.3", {"start": v(278.24, -37.61) * mm, "end": v(279.47, -39.75) * mm});
            skLineSegment(sketch, "E115.1.4", {"start": v(305.95, -21.61) * mm, "end": v(307.19, -23.75) * mm});
            skLineSegment(sketch, "E115.1.5", {"start": v(299.02, -25.61) * mm, "end": v(305.95, -21.61) * mm});
            skLineSegment(sketch, "E115.1.6", {"start": v(301.52, -29.94) * mm, "end": v(299.02, -25.61) * mm});
            skLineSegment(sketch, "E115.2.1", {"start": v(299.02, 25.61) * mm, "end": v(305.95, 21.61) * mm});
            skLineSegment(sketch, "E115.2.2", {"start": v(301.52, 29.94) * mm, "end": v(299.02, 25.61) * mm});
            skLineSegment(sketch, "E115.2.3", {"start": v(305.95, 21.61) * mm, "end": v(307.19, 23.75) * mm});
            skLineSegment(sketch, "E115.2.4", {"start": v(278.24, 37.61) * mm, "end": v(279.47, 39.75) * mm});
            skLineSegment(sketch, "E115.2.5", {"start": v(285.17, 33.61) * mm, "end": v(278.24, 37.61) * mm});
            skLineSegment(sketch, "E115.2.6", {"start": v(287.67, 37.94) * mm, "end": v(285.17, 33.61) * mm});
            skArc(sketch, "E116", {"start": v(279.47, 39.75) * mm, "mid": v(255, 34.64) * mm, "end": v(238.34, 16) * mm});
            skArc(sketch, "E117.trimOffspring", {"start": v(301.52, 29.94) * mm, "mid": v(295, 34.64) * mm, "end": v(287.67, 37.94) * mm});
            skArc(sketch, "E118.trimOffspring", {"start": v(307.19, -23.75) * mm, "mid": v(315, 0) * mm, "end": v(307.19, 23.75) * mm});
            skArc(sketch, "E119.trimOffspring", {"start": v(287.67, -37.94) * mm, "mid": v(295, -34.64) * mm, "end": v(301.52, -29.94) * mm});
            skArc(sketch, "E120.trimOffspring", {"start": v(238.34, -16) * mm, "mid": v(255, -34.64) * mm, "end": v(279.47, -39.75) * mm});
            skArc(sketch, "E121.trimOffspring", {"start": v(235.8, 8) * mm, "mid": v(235, 0) * mm, "end": v(235.8, -8) * mm});
            skLineSegment(sketch, "E122.0", {"start": v(185, 8) * mm, "end": v(175, 8) * mm, "construction": true});
            skLineSegment(sketch, "E123", {"start": v(185, 8) * mm, "end": v(185, -8) * mm, "construction": true});
            skLineSegment(sketch, "E124", {"start": v(185, -8) * mm, "end": v(175, -8) * mm, "construction": true});
            skLineSegment(sketch, "E125", {"start": v(175, -8) * mm, "end": v(175, 8) * mm, "construction": true});
            skSolve(sketch);
        }
        {
            var Q0;
            Q0=makeQuery(id+"F24.imprint","IMPRINT",FACE,{"disambiguationData":[TD([[makeQuery(id+"F24.imprint","IMPRINT",EDGE,{"derivedFrom":sQuery(id+"F24.wireOp",EDGE,"E109")}),1.0]])]});
            var Q1;
            Q1=sQuery(id+"F24.wireOp",EDGE,"E110");
            extrude(context, id + "F25", {"entities" : qUnion([Q0]), "surfaceEntities" : qUnion([Q1]), "depth" : 8 * mm, "offsetDistance" : 25 * mm});
        }
        {
            var Q0;
            Q0=qCreatedBy(makeId("Top.planeOp"),FACE);
            cPlane(context, id + "F26", {"entities" : qUnion([Q0]), "cplaneType" : CPlaneType.OFFSET, "offset" : 100 * mm, "oppositeDirection" : true, "width" : 150 * mm, "height" : 150 * mm});
        }
        {
            var Q0;
            Q0=makeQuery(id+"F25.opExtrude","SWEPT_BODY",BODY,{"disambiguationData":[OSD([sQuery(id+"F24.wireOp",EDGE,"E109"),sQuery(id+"F24.wireOp",EDGE,"E110"),sQuery(id+"F24.wireOp",EDGE,"E111"),sQuery(id+"F24.wireOp",EDGE,"E112.MirrorCS"),sQuery(id+"F24.wireOp",EDGE,"E113.MirrorCS"),sQuery(id+"F24.wireOp",EDGE,"E114.MirrorCS"),sQuery(id+"F24.wireOp",EDGE,"E115.1.1"),sQuery(id+"F24.wireOp",EDGE,"E115.1.2"),sQuery(id+"F24.wireOp",EDGE,"E115.1.3"),sQuery(id+"F24.wireOp",EDGE,"E115.1.4"),sQuery(id+"F24.wireOp",EDGE,"E115.1.5"),sQuery(id+"F24.wireOp",EDGE,"E115.1.6"),sQuery(id+"F24.wireOp",EDGE,"E107"),sQuery(id+"F24.wireOp",EDGE,"E115.2.1"),sQuery(id+"F24.wireOp",EDGE,"E115.2.2"),sQuery(id+"F24.wireOp",EDGE,"E115.2.3"),sQuery(id+"F24.wireOp",EDGE,"E115.2.4"),sQuery(id+"F24.wireOp",EDGE,"E115.2.5"),sQuery(id+"F24.wireOp",EDGE,"E115.2.6"),sQuery(id+"F24.wireOp",EDGE,"E116"),sQuery(id+"F24.wireOp",EDGE,"E117.trimOffspring"),sQuery(id+"F24.wireOp",EDGE,"E118.trimOffspring"),sQuery(id+"F24.wireOp",EDGE,"E119.trimOffspring"),sQuery(id+"F24.wireOp",EDGE,"E120.trimOffspring"),sQuery(id+"F24.wireOp",EDGE,"E121.trimOffspring")])]});
            transform(context, id + "F27", {"entities" : qUnion([Q0]), "transformType" : TransformType.TRANSLATION_3D, "dx" : 2 * mm, "dy" : 0 * mm, "dz" : 0 * mm, "makeCopy" : false});
        }
        {
            var Q0;
            Q0=makeQuery(id+"F25.opExtrude","SWEPT_FACE",FACE,{"disambiguationData":[OSD([sQuery(id+"F24.wireOp",EDGE,"E115.1.2")])]});
            cPlane(context, id + "F28", {"entities" : qUnion([Q0]), "cplaneType" : CPlaneType.OFFSET, "offset" : 8 * mm, "oppositeDirection" : true, "width" : 150 * mm, "height" : 150 * mm});
        }
        {
            var Q0;
            Q0=makeQuery(id+"F25.opExtrude","SWEPT_FACE",FACE,{"disambiguationData":[OSD([sQuery(id+"F24.wireOp",EDGE,"E115.2.2")])]});
            cPlane(context, id + "F29", {"entities" : qUnion([Q0]), "cplaneType" : CPlaneType.OFFSET, "offset" : 8 * mm, "oppositeDirection" : true, "width" : 150 * mm, "height" : 150 * mm});
        }
        {
            var Q0;
            Q0=qCreatedBy(id+"F26.planeOp",FACE);
            var sketch = newSketch(context, id + "F30", { "sketchPlane" : qUnion([Q0])});
            skCircle(sketch, "E126.0", {"center": v(277, 0) * mm, "radius": 20.5 * mm, "construction": true});
            skCircle(sketch, "E127", {"center": v(277, 0) * mm, "radius": 87.5 * mm});
            skArc(sketch, "E128", {"start": v(178.29, -16) * mm, "mid": v(227, -86.6) * mm, "end": v(312.5, -93.49) * mm});
            skLineSegment(sketch, "E129.0", {"start": v(177.32, -8) * mm, "end": v(182.32, -8) * mm});
            skLineSegment(sketch, "E130.0", {"start": v(182.32, -8) * mm, "end": v(182.32, -16) * mm});
            skLineSegment(sketch, "E131", {"start": v(182.32, -16) * mm, "end": v(178.29, -16) * mm});
            skLineSegment(sketch, "E132.MirrorCS", {"start": v(182.32, 8) * mm, "end": v(182.32, 16) * mm});
            skLineSegment(sketch, "E133.MirrorCS", {"start": v(182.32, 16) * mm, "end": v(178.29, 16) * mm});
            skLineSegment(sketch, "E134.MirrorCS", {"start": v(177.32, 8) * mm, "end": v(182.32, 8) * mm});
            skArc(sketch, "E135.trimOffspring", {"start": v(177.32, 8) * mm, "mid": v(177, 0) * mm, "end": v(177.32, -8) * mm});
            skLineSegment(sketch, "E136.1.0", {"start": v(317.41, -86) * mm, "end": v(310.48, -90) * mm});
            skLineSegment(sketch, "E136.1.1", {"start": v(310.48, -90) * mm, "end": v(312.5, -93.49) * mm});
            skLineSegment(sketch, "E136.1.2", {"start": v(319.91, -90.32) * mm, "end": v(317.41, -86) * mm});
            skLineSegment(sketch, "E136.1.3", {"start": v(333.77, -82.32) * mm, "end": v(331.27, -78) * mm});
            skLineSegment(sketch, "E136.1.4", {"start": v(331.27, -78) * mm, "end": v(338.2, -74) * mm});
            skLineSegment(sketch, "E136.1.5", {"start": v(338.2, -74) * mm, "end": v(340.21, -77.49) * mm});
            skLineSegment(sketch, "E136.2.0", {"start": v(331.27, 78) * mm, "end": v(338.2, 74) * mm});
            skLineSegment(sketch, "E136.2.1", {"start": v(338.2, 74) * mm, "end": v(340.21, 77.49) * mm});
            skLineSegment(sketch, "E136.2.2", {"start": v(333.77, 82.32) * mm, "end": v(331.27, 78) * mm});
            skLineSegment(sketch, "E136.2.3", {"start": v(319.91, 90.32) * mm, "end": v(317.41, 86) * mm});
            skLineSegment(sketch, "E136.2.4", {"start": v(317.41, 86) * mm, "end": v(310.48, 90) * mm});
            skLineSegment(sketch, "E136.2.5", {"start": v(310.48, 90) * mm, "end": v(312.5, 93.49) * mm});
            skArc(sketch, "E137.trimOffspring", {"start": v(312.5, 93.49) * mm, "mid": v(227, 86.6) * mm, "end": v(178.29, 16) * mm});
            skArc(sketch, "E138.trimOffspring", {"start": v(333.77, 82.32) * mm, "mid": v(327, 86.6) * mm, "end": v(319.91, 90.32) * mm});
            skArc(sketch, "E139.trimOffspring", {"start": v(340.21, -77.49) * mm, "mid": v(377, 0) * mm, "end": v(340.21, 77.49) * mm});
            skArc(sketch, "E140.trimOffspring", {"start": v(319.91, -90.32) * mm, "mid": v(327, -86.6) * mm, "end": v(333.77, -82.32) * mm});
            skSolve(sketch);
        }
        {
            var Q0;
            Q0 = qSketchRegion(id + "F30", true);
            extrude(context, id + "F31", {"entities" : qUnion([Q0]), "oppositeDirection" : true, "depth" : 8 * mm, "offsetDistance" : 25 * mm});
        }
        {
            var Q0;
            Q0=makeQuery(id+"F20.opExtrude","CAP_FACE",FACE,{"disambiguationData":[OSD([sQuery(id+"F19.wireOp",EDGE,"E86.top"),sQuery(id+"F19.wireOp",EDGE,"E86.left"),sQuery(id+"F19.wireOp",EDGE,"E86.right"),sQuery(id+"F19.wireOp",EDGE,"E89.MirrorC"),sQuery(id+"F19.wireOp",EDGE,"E90.filletArc"),sQuery(id+"F19.wireOp",EDGE,"E91.filletArc"),sQuery(id+"F19.wireOp",EDGE,"E92.bottom"),sQuery(id+"F19.wireOp",EDGE,"E93"),sQuery(id+"F19.wireOp",EDGE,"E94.filletArc"),sQuery(id+"F19.wireOp",EDGE,"E95.filletArc")])],"isStart":false});
            var sketch = newSketch(context, id + "F32", { "sketchPlane" : qUnion([Q0])});
            skLineSegment(sketch, "E141.top", {"start": v(170, -5) * mm, "end": v(170, 5) * mm});
            skLineSegment(sketch, "E141.left", {"start": v(191.07, -10) * mm, "end": v(175, -10) * mm});
            skLineSegment(sketch, "E141.right", {"start": v(203.17, 10) * mm, "end": v(175, 10) * mm});
            skCircle(sketch, "E142.MirrorC", {"center": v(180, 0) * mm, "radius": 5 * mm});
            skPoint(sketch, "E143.visualSharp", {"position": v(170, -10) * mm});
            skArc(sketch, "E143.filletArc", {"start": v(170, -5) * mm, "mid": v(171.46, -8.54) * mm, "end": v(175, -10) * mm});
            skPoint(sketch, "E144.visualSharp", {"position": v(170, 10) * mm});
            skArc(sketch, "E144.filletArc", {"start": v(175, 10) * mm, "mid": v(171.46, 8.54) * mm, "end": v(170, 5) * mm});
            skLineSegment(sketch, "E145", {"start": v(237.8, 100) * mm, "end": v(212.74, 17.1) * mm});
            skLineSegment(sketch, "E146.trimOffspring", {"start": v(200.64, -22.9) * mm, "end": v(177.32, -100) * mm});
            skLineSegment(sketch, "E147", {"start": v(237.8, 100) * mm, "end": v(237.8, 115) * mm});
            skLineSegment(sketch, "E148", {"start": v(242.8, 120) * mm, "end": v(242.8, 120) * mm});
            skLineSegment(sketch, "E149", {"start": v(247.8, 115) * mm, "end": v(247.8, 108) * mm});
            skLineSegment(sketch, "E150", {"start": v(247.8, 100) * mm, "end": v(187.32, -100) * mm});
            skLineSegment(sketch, "E151", {"start": v(182.32, -120) * mm, "end": v(182.32, -120) * mm});
            skLineSegment(sketch, "E152.0.2", {"start": v(242.8, 108) * mm, "end": v(237.8, 108) * mm, "construction": true});
            skLineSegment(sketch, "E152.0.3", {"start": v(237.8, 108) * mm, "end": v(237.8, 100) * mm, "construction": true});
            skPoint(sketch, "E153.visualSharp", {"position": v(210.59, 10) * mm});
            skArc(sketch, "E153.filletArc", {"start": v(203.17, 10) * mm, "mid": v(209.13, 11.97) * mm, "end": v(212.74, 17.1) * mm});
            skPoint(sketch, "E154.visualSharp", {"position": v(204.54, -10) * mm});
            skArc(sketch, "E154.filletArc", {"start": v(200.64, -22.9) * mm, "mid": v(199.1, -14.04) * mm, "end": v(191.07, -10) * mm});
            skPoint(sketch, "E155.visualSharp", {"position": v(177.32, -120) * mm});
            skArc(sketch, "E155.filletArc", {"start": v(177.32, -115) * mm, "mid": v(178.78, -118.54) * mm, "end": v(182.32, -120) * mm});
            skPoint(sketch, "E156.visualSharp", {"position": v(187.32, -120) * mm});
            skArc(sketch, "E156.filletArc", {"start": v(182.32, -120) * mm, "mid": v(185.86, -118.54) * mm, "end": v(187.32, -115) * mm});
            skPoint(sketch, "E157.visualSharp", {"position": v(237.8, 120) * mm});
            skArc(sketch, "E157.filletArc", {"start": v(242.8, 120) * mm, "mid": v(239.27, 118.54) * mm, "end": v(237.8, 115) * mm});
            skPoint(sketch, "E158.visualSharp", {"position": v(247.8, 120) * mm});
            skArc(sketch, "E158.filletArc", {"start": v(247.8, 115) * mm, "mid": v(246.34, 118.54) * mm, "end": v(242.8, 120) * mm});
            skLineSegment(sketch, "E159", {"start": v(247.8, 108) * mm, "end": v(242.8, 108) * mm});
            skLineSegment(sketch, "E160", {"start": v(242.8, 108) * mm, "end": v(242.8, 100) * mm});
            skLineSegment(sketch, "E161", {"start": v(242.8, 100) * mm, "end": v(247.8, 100) * mm});
            skLineSegment(sketch, "E162", {"start": v(187.32, -100) * mm, "end": v(182.32, -100) * mm});
            skLineSegment(sketch, "E163", {"start": v(182.32, -100) * mm, "end": v(182.32, -108) * mm});
            skLineSegment(sketch, "E164", {"start": v(182.32, -108) * mm, "end": v(187.32, -108) * mm});
            skLineSegment(sketch, "E165.0.0", {"start": v(182.32, -100) * mm, "end": v(177.32, -100) * mm, "construction": true});
            skLineSegment(sketch, "E165.0.1", {"start": v(177.32, -100) * mm, "end": v(177.32, -108) * mm, "construction": true});
            skLineSegment(sketch, "E165.0.2", {"start": v(177.32, -108) * mm, "end": v(182.32, -108) * mm, "construction": true});
            skLineSegment(sketch, "E165.0.3", {"start": v(182.32, -108) * mm, "end": v(182.32, -100) * mm, "construction": true});
            skLineSegment(sketch, "E166", {"start": v(177.32, -100) * mm, "end": v(177.32, -115) * mm});
            skLineSegment(sketch, "E167", {"start": v(187.32, -108) * mm, "end": v(187.32, -115) * mm});
            skSolve(sketch);
        }
        {
            var Q0;
            Q0 = qSketchRegion(id + "F32", true);
            extrude(context, id + "F33", {"entities" : qUnion([Q0]), "depth" : 8 * mm, "offsetDistance" : 25 * mm});
        }
        {
            var Q0;
            Q0=makeQuery(id+"F33.opExtrude","SWEPT_BODY",BODY,{"disambiguationData":[OSD([sQuery(id+"F32.wireOp",EDGE,"E141.top"),sQuery(id+"F32.wireOp",EDGE,"E141.left"),sQuery(id+"F32.wireOp",EDGE,"E141.right"),sQuery(id+"F32.wireOp",EDGE,"E142.MirrorC"),sQuery(id+"F32.wireOp",EDGE,"E143.filletArc"),sQuery(id+"F32.wireOp",EDGE,"E144.filletArc"),sQuery(id+"F32.wireOp",EDGE,"E145"),sQuery(id+"F32.wireOp",EDGE,"E146.trimOffspring"),sQuery(id+"F32.wireOp",EDGE,"E147"),sQuery(id+"F32.wireOp",EDGE,"E149"),sQuery(id+"F32.wireOp",EDGE,"E150"),sQuery(id+"F32.wireOp",EDGE,"vQYsRbkT-yidu-s9Dx-8HfP-1cVZBKzJqOnp"),sQuery(id+"F32.wireOp",EDGE,"Z77I2Dmk-SxWq-cxIy-LfgW-7D05WhU1y4ug"),sQuery(id+"F32.wireOp",EDGE,"6ed29332-a8b3-43e6-a333-3f3c8759dfa2"),sQuery(id+"F32.wireOp",EDGE,"E153.filletArc"),sQuery(id+"F32.wireOp",EDGE,"E154.filletArc"),sQuery(id+"F32.wireOp",EDGE,"E155.filletArc"),sQuery(id+"F32.wireOp",EDGE,"E156.filletArc"),sQuery(id+"F32.wireOp",EDGE,"E157.filletArc"),sQuery(id+"F32.wireOp",EDGE,"E158.filletArc"),sQuery(id+"F32.wireOp",EDGE,"E159"),sQuery(id+"F32.wireOp",EDGE,"E160"),sQuery(id+"F32.wireOp",EDGE,"E161"),sQuery(id+"F32.wireOp",EDGE,"E162"),sQuery(id+"F32.wireOp",EDGE,"E163"),sQuery(id+"F32.wireOp",EDGE,"E164")])]});
            var Q1;
            Q1=qCreatedBy(makeId("Front.planeOp"),FACE);
            mirror(context, id + "F34", {"entities" : qUnion([Q0]), "mirrorPlane" : qUnion([Q1])});
        }
        {
            var Q0;
            Q0=makeQuery(id+"F25.opExtrude","SWEPT_FACE",FACE,{"disambiguationData":[OSD([sQuery(id+"F24.wireOp",EDGE,"E115.1.6")])]});
            var sketch = newSketch(context, id + "F35", { "sketchPlane" : qUnion([Q0])});
            skLineSegment(sketch, "E168", {"start": v(-177.7, 100) * mm, "end": v(-177.7, 115) * mm});
            skLineSegment(sketch, "E169", {"start": v(-133.8, 233.57) * mm, "end": v(-133.8, 233.57) * mm});
            skLineSegment(sketch, "E170", {"start": v(-167.7, 115) * mm, "end": v(-167.7, 108) * mm});
            skLineSegment(sketch, "E171", {"start": v(-167.7, 100) * mm, "end": v(-228.18, -100) * mm});
            skLineSegment(sketch, "E172.0.2", {"start": v(-172.7, 108) * mm, "end": v(-177.7, 108) * mm, "construction": true});
            skLineSegment(sketch, "E172.0.3", {"start": v(-177.7, 108) * mm, "end": v(-177.7, 100) * mm, "construction": true});
            skPoint(sketch, "E173.visualSharp", {"position": v(-238.18, -120) * mm});
            skArc(sketch, "E173.filletArc", {"start": v(-238.18, -115) * mm, "mid": v(-236.72, -118.54) * mm, "end": v(-233.18, -120) * mm});
            skPoint(sketch, "E174.visualSharp", {"position": v(-228.18, -120) * mm});
            skArc(sketch, "E174.filletArc", {"start": v(-233.18, -120) * mm, "mid": v(-229.64, -118.54) * mm, "end": v(-228.18, -115) * mm});
            skPoint(sketch, "E175.visualSharp", {"position": v(-177.7, 120) * mm});
            skArc(sketch, "E175.filletArc", {"start": v(-172.7, 120) * mm, "mid": v(-176.23, 118.54) * mm, "end": v(-177.7, 115) * mm});
            skPoint(sketch, "E176.visualSharp", {"position": v(-167.7, 120) * mm});
            skArc(sketch, "E176.filletArc", {"start": v(-167.7, 115) * mm, "mid": v(-169.16, 118.54) * mm, "end": v(-172.7, 120) * mm});
            skLineSegment(sketch, "E177", {"start": v(-167.7, 108) * mm, "end": v(-172.7, 108) * mm});
            skLineSegment(sketch, "E178", {"start": v(-172.7, 108) * mm, "end": v(-172.7, 100) * mm});
            skLineSegment(sketch, "E179", {"start": v(-172.7, 100) * mm, "end": v(-167.7, 100) * mm});
            skLineSegment(sketch, "E180", {"start": v(-228.18, -100) * mm, "end": v(-233.18, -100) * mm});
            skLineSegment(sketch, "E181", {"start": v(-233.18, -100) * mm, "end": v(-233.18, -108) * mm});
            skLineSegment(sketch, "E182", {"start": v(-233.18, -108) * mm, "end": v(-228.18, -108) * mm});
            skLineSegment(sketch, "E183.0.0", {"start": v(-233.18, -100) * mm, "end": v(-238.18, -100) * mm, "construction": true});
            skLineSegment(sketch, "E183.0.1", {"start": v(-238.18, -100) * mm, "end": v(-238.18, -108) * mm, "construction": true});
            skLineSegment(sketch, "E183.0.2", {"start": v(-238.18, -108) * mm, "end": v(-233.18, -108) * mm, "construction": true});
            skLineSegment(sketch, "E183.0.3", {"start": v(-233.18, -108) * mm, "end": v(-233.18, -100) * mm, "construction": true});
            skLineSegment(sketch, "E184", {"start": v(-238.18, -100) * mm, "end": v(-238.18, -115) * mm});
            skLineSegment(sketch, "E185", {"start": v(-228.18, -108) * mm, "end": v(-228.18, -115) * mm});
            skLineSegment(sketch, "E186", {"start": v(-177.7, 100) * mm, "end": v(-238.18, -100) * mm});
            skSolve(sketch);
        }
        {
            var Q0;
            Q0 = qSketchRegion(id + "F35", true);
            extrude(context, id + "F36", {"entities" : qUnion([Q0]), "depth" : 8 * mm, "offsetDistance" : 25 * mm});
        }
        {
            var Q0;
            Q0=makeQuery(id+"F25.opExtrude","SWEPT_FACE",FACE,{"disambiguationData":[OSD([sQuery(id+"F24.wireOp",EDGE,"E115.2.6")])]});
            var sketch = newSketch(context, id + "F37", { "sketchPlane" : qUnion([Q0])});
            skLineSegment(sketch, "E187", {"start": v(-177.7, 100) * mm, "end": v(-177.7, 115) * mm});
            skLineSegment(sketch, "E188", {"start": v(-154.81, 239.13) * mm, "end": v(-154.81, 239.13) * mm});
            skLineSegment(sketch, "E189", {"start": v(-167.7, 115) * mm, "end": v(-167.7, 108) * mm});
            skLineSegment(sketch, "E190", {"start": v(-167.7, 100) * mm, "end": v(-228.18, -100) * mm});
            skLineSegment(sketch, "E191.0.2", {"start": v(-172.7, 108) * mm, "end": v(-177.7, 108) * mm, "construction": true});
            skLineSegment(sketch, "E191.0.3", {"start": v(-177.7, 108) * mm, "end": v(-177.7, 100) * mm, "construction": true});
            skPoint(sketch, "E192.visualSharp", {"position": v(-238.18, -120) * mm});
            skArc(sketch, "E192.filletArc", {"start": v(-238.18, -115) * mm, "mid": v(-236.72, -118.54) * mm, "end": v(-233.18, -120) * mm});
            skPoint(sketch, "E193.visualSharp", {"position": v(-228.18, -120) * mm});
            skArc(sketch, "E193.filletArc", {"start": v(-233.18, -120) * mm, "mid": v(-229.64, -118.54) * mm, "end": v(-228.18, -115) * mm});
            skPoint(sketch, "E194.visualSharp", {"position": v(-177.7, 120) * mm});
            skArc(sketch, "E194.filletArc", {"start": v(-172.7, 120) * mm, "mid": v(-176.23, 118.54) * mm, "end": v(-177.7, 115) * mm});
            skPoint(sketch, "E195.visualSharp", {"position": v(-167.7, 120) * mm});
            skArc(sketch, "E195.filletArc", {"start": v(-167.7, 115) * mm, "mid": v(-169.16, 118.54) * mm, "end": v(-172.7, 120) * mm});
            skLineSegment(sketch, "E196", {"start": v(-167.7, 108) * mm, "end": v(-172.7, 108) * mm});
            skLineSegment(sketch, "E197", {"start": v(-172.7, 108) * mm, "end": v(-172.7, 100) * mm});
            skLineSegment(sketch, "E198", {"start": v(-172.7, 100) * mm, "end": v(-167.7, 100) * mm});
            skLineSegment(sketch, "E199", {"start": v(-228.18, -100) * mm, "end": v(-233.18, -100) * mm});
            skLineSegment(sketch, "E200", {"start": v(-233.18, -100) * mm, "end": v(-233.18, -108) * mm});
            skLineSegment(sketch, "E201", {"start": v(-233.18, -108) * mm, "end": v(-228.18, -108) * mm});
            skLineSegment(sketch, "E202.0.0", {"start": v(-233.18, -100) * mm, "end": v(-238.18, -100) * mm, "construction": true});
            skLineSegment(sketch, "E202.0.1", {"start": v(-238.18, -100) * mm, "end": v(-238.18, -108) * mm, "construction": true});
            skLineSegment(sketch, "E202.0.2", {"start": v(-238.18, -108) * mm, "end": v(-233.18, -108) * mm, "construction": true});
            skLineSegment(sketch, "E202.0.3", {"start": v(-233.18, -108) * mm, "end": v(-233.18, -100) * mm, "construction": true});
            skLineSegment(sketch, "E203", {"start": v(-238.18, -100) * mm, "end": v(-238.18, -115) * mm});
            skLineSegment(sketch, "E204", {"start": v(-228.18, -108) * mm, "end": v(-228.18, -115) * mm});
            skLineSegment(sketch, "E205", {"start": v(-238.18, -100) * mm, "end": v(-177.7, 100) * mm});
            skSolve(sketch);
        }
        {
            var Q0;
            Q0 = qSketchRegion(id + "F37", true);
            extrude(context, id + "F38", {"entities" : qUnion([Q0]), "depth" : 8 * mm, "offsetDistance" : 25 * mm});
        }
        {
            var Q0;
            Q0=makeQuery(id+"F38.opExtrude","SWEPT_BODY",BODY,{"disambiguationData":[OSD([sQuery(id+"F37.wireOp",EDGE,"E187"),sQuery(id+"F37.wireOp",EDGE,"E189"),sQuery(id+"F37.wireOp",EDGE,"E190"),sQuery(id+"F37.wireOp",EDGE,"E192.filletArc"),sQuery(id+"F37.wireOp",EDGE,"E193.filletArc"),sQuery(id+"F37.wireOp",EDGE,"E194.filletArc"),sQuery(id+"F37.wireOp",EDGE,"E195.filletArc"),sQuery(id+"F37.wireOp",EDGE,"E196"),sQuery(id+"F37.wireOp",EDGE,"E197"),sQuery(id+"F37.wireOp",EDGE,"E198"),sQuery(id+"F37.wireOp",EDGE,"E199"),sQuery(id+"F37.wireOp",EDGE,"E200"),sQuery(id+"F37.wireOp",EDGE,"E203"),sQuery(id+"F37.wireOp",EDGE,"E201"),sQuery(id+"F37.wireOp",EDGE,"E204"),sQuery(id+"F37.wireOp",EDGE,"E205")])]});
            var Q1;
            Q1=qCreatedBy(id+"F29.planeOp",FACE);
            mirror(context, id + "F39", {"entities" : qUnion([Q0]), "mirrorPlane" : qUnion([Q1])});
        }
        {
            var Q0;
            Q0=makeQuery(id+"F36.opExtrude","SWEPT_BODY",BODY,{"disambiguationData":[OSD([sQuery(id+"F35.wireOp",EDGE,"E168"),sQuery(id+"F35.wireOp",EDGE,"E170"),sQuery(id+"F35.wireOp",EDGE,"E171"),sQuery(id+"F35.wireOp",EDGE,"E173.filletArc"),sQuery(id+"F35.wireOp",EDGE,"E174.filletArc"),sQuery(id+"F35.wireOp",EDGE,"E175.filletArc"),sQuery(id+"F35.wireOp",EDGE,"E176.filletArc"),sQuery(id+"F35.wireOp",EDGE,"E177"),sQuery(id+"F35.wireOp",EDGE,"E178"),sQuery(id+"F35.wireOp",EDGE,"E179"),sQuery(id+"F35.wireOp",EDGE,"E180"),sQuery(id+"F35.wireOp",EDGE,"E181"),sQuery(id+"F35.wireOp",EDGE,"E184"),sQuery(id+"F35.wireOp",EDGE,"E182"),sQuery(id+"F35.wireOp",EDGE,"E185"),sQuery(id+"F35.wireOp",EDGE,"E186")])]});
            var Q1;
            Q1=qCreatedBy(id+"F28.planeOp",FACE);
            mirror(context, id + "F40", {"entities" : qUnion([Q0]), "mirrorPlane" : qUnion([Q1])});
        }
    });
